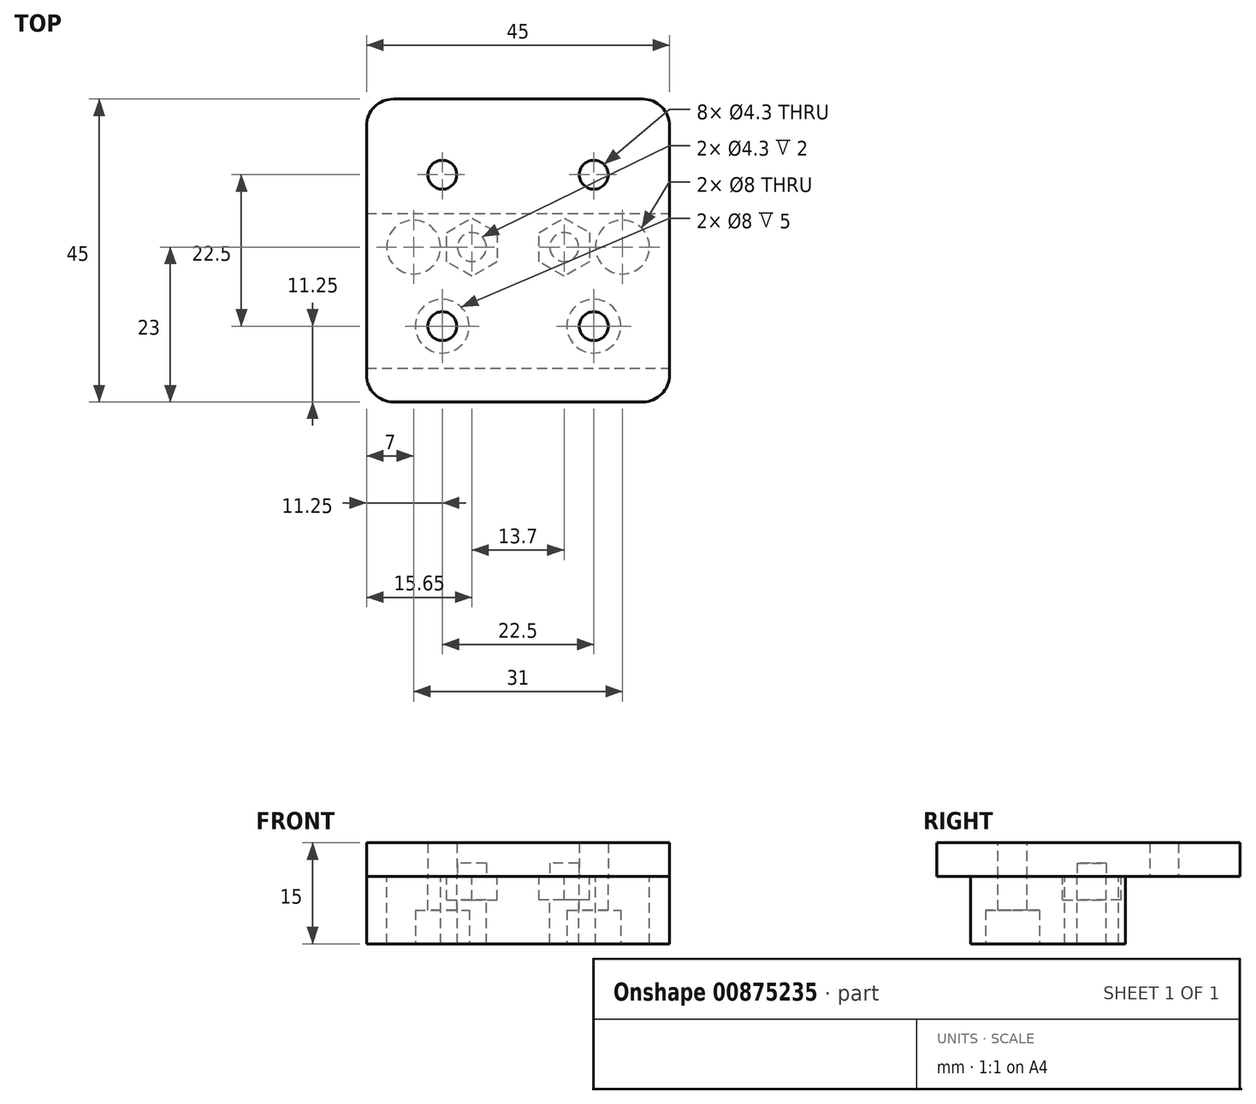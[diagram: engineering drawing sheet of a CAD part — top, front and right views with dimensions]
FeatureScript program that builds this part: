
annotation { "Feature Type Name" : "Feature", "Feature Type Description" : "" }
export const myFeature = defineFeature(function(context is Context, id is Id, definition is map)
    precondition{}
    {
        {
            var Q0;
            Q0=qCreatedBy(makeId("Top.planeOp"),FACE);
            var sketch = newSketch(context, id + "F0", { "sketchPlane" : qUnion([Q0])});
            skLineSegment(sketch, "E0.bottom", {"start": v(5, -5) * mm, "end": v(50, -5) * mm});
            skLineSegment(sketch, "E1", {"start": v(27.5, 40) * mm, "end": v(27.5, -5) * mm, "construction": true});
            skLineSegment(sketch, "E2.bottom", {"start": v(9, -5) * mm, "end": v(46, -5) * mm});
            skLineSegment(sketch, "E2.top", {"start": v(9, 40) * mm, "end": v(46, 40) * mm});
            skLineSegment(sketch, "E2.left", {"start": v(5, -1) * mm, "end": v(5, 36) * mm});
            skLineSegment(sketch, "E2.right", {"start": v(50, -1) * mm, "end": v(50, 36) * mm});
            skLineSegment(sketch, "E3", {"start": v(18.4, 28.75) * mm, "end": v(36.6, 28.75) * mm, "construction": true});
            skLineSegment(sketch, "E4", {"start": v(38.75, 26.6) * mm, "end": v(38.75, 8.4) * mm, "construction": true});
            skLineSegment(sketch, "E5", {"start": v(36.6, 6.25) * mm, "end": v(18.4, 6.25) * mm, "construction": true});
            skLineSegment(sketch, "E6", {"start": v(16.25, 8.4) * mm, "end": v(16.25, 26.6) * mm, "construction": true});
            skPoint(sketch, "E7", {"position": v(27.5, 28.75) * mm});
            skPoint(sketch, "E8", {"position": v(27.5, 6.25) * mm});
            skPoint(sketch, "E9", {"position": v(50, 17.5) * mm});
            skPoint(sketch, "E10", {"position": v(5, 17.5) * mm});
            skLineSegment(sketch, "E11", {"start": v(5, 17.5) * mm, "end": v(50, 17.5) * mm, "construction": true});
            skPoint(sketch, "E12", {"position": v(16.25, 17.5) * mm});
            skPoint(sketch, "E13", {"position": v(38.75, 17.5) * mm});
            skCircle(sketch, "E14", {"center": v(16.25, 28.75) * mm, "radius": 2.15 * mm});
            skCircle(sketch, "E15", {"center": v(38.75, 6.25) * mm, "radius": 2.15 * mm});
            skCircle(sketch, "E16", {"center": v(16.25, 6.25) * mm, "radius": 2.15 * mm});
            skCircle(sketch, "E17", {"center": v(38.75, 28.75) * mm, "radius": 2.15 * mm});
            skPoint(sketch, "E18.visualSharp", {"position": v(5, 40) * mm});
            skArc(sketch, "E18.filletArc", {"start": v(9, 40) * mm, "mid": v(6.17, 38.83) * mm, "end": v(5, 36) * mm});
            skPoint(sketch, "E19.visualSharp", {"position": v(50, 40) * mm});
            skArc(sketch, "E19.filletArc", {"start": v(50, 36) * mm, "mid": v(48.83, 38.83) * mm, "end": v(46, 40) * mm});
            skPoint(sketch, "E20.visualSharp", {"position": v(50, -5) * mm});
            skArc(sketch, "E20.filletArc", {"start": v(46, -5) * mm, "mid": v(48.83, -3.83) * mm, "end": v(50, -1) * mm});
            skPoint(sketch, "E21.visualSharp", {"position": v(5, -5) * mm});
            skArc(sketch, "E21.filletArc", {"start": v(5, -1) * mm, "mid": v(6.17, -3.83) * mm, "end": v(9, -5) * mm});
            skSolve(sketch);
        }
        {
            var Q0;
            Q0=qCreatedBy(makeId("Top.planeOp"),FACE);
            var sketch = newSketch(context, id + "F1", { "sketchPlane" : qUnion([Q0])});
            skLineSegment(sketch, "E22.bottom", {"start": v(5, 0) * mm, "end": v(50, 0) * mm});
            skLineSegment(sketch, "E22.top", {"start": v(5, 23) * mm, "end": v(50, 23) * mm});
            skLineSegment(sketch, "E23", {"start": v(27.5, 23) * mm, "end": v(27.5, -48.49) * mm, "construction": true});
            skCircle(sketch, "E24", {"center": v(34.35, 18) * mm, "radius": 2.15 * mm});
            skCircle(sketch, "E25", {"center": v(20.65, 18) * mm, "radius": 2.15 * mm});
            skCircle(sketch, "E26", {"center": v(43, 18) * mm, "radius": 4 * mm});
            skCircle(sketch, "E27", {"center": v(12, 18) * mm, "radius": 4 * mm});
            skCircle(sketch, "E28.cCircle", {"center": v(20.65, 18) * mm, "radius": 3.75 * mm, "construction": true});
            skLineSegment(sketch, "E28.0", {"start": v(24.4, 20.17) * mm, "end": v(24.4, 15.83) * mm});
            skLineSegment(sketch, "E28.1", {"start": v(24.4, 15.83) * mm, "end": v(20.65, 13.67) * mm});
            skLineSegment(sketch, "E28.2", {"start": v(20.65, 13.67) * mm, "end": v(16.9, 15.83) * mm});
            skLineSegment(sketch, "E28.3", {"start": v(16.9, 15.83) * mm, "end": v(16.9, 20.17) * mm});
            skLineSegment(sketch, "E28.4", {"start": v(16.9, 20.17) * mm, "end": v(20.65, 22.33) * mm});
            skLineSegment(sketch, "E28.5", {"start": v(20.65, 22.33) * mm, "end": v(24.4, 20.17) * mm});
            skPoint(sketch, "E28.0.midPoint", {"position": v(24.4, 18) * mm});
            skCircle(sketch, "E29.cCircle", {"center": v(34.35, 18) * mm, "radius": 3.75 * mm, "construction": true});
            skLineSegment(sketch, "E29.0", {"start": v(30.6, 15.83) * mm, "end": v(30.6, 20.17) * mm});
            skLineSegment(sketch, "E29.1", {"start": v(30.6, 20.17) * mm, "end": v(34.35, 22.33) * mm});
            skLineSegment(sketch, "E29.2", {"start": v(34.35, 22.33) * mm, "end": v(38.1, 20.17) * mm});
            skLineSegment(sketch, "E29.3", {"start": v(38.1, 20.17) * mm, "end": v(38.1, 15.83) * mm});
            skLineSegment(sketch, "E29.4", {"start": v(38.1, 15.83) * mm, "end": v(34.35, 13.67) * mm});
            skLineSegment(sketch, "E29.5", {"start": v(34.35, 13.67) * mm, "end": v(30.6, 15.83) * mm});
            skPoint(sketch, "E29.0.midPoint", {"position": v(30.6, 18) * mm});
            skLineSegment(sketch, "E30.0", {"start": v(5, -1) * mm, "end": v(5, 36) * mm, "construction": true});
            skLineSegment(sketch, "E31.0", {"start": v(50, -1) * mm, "end": v(50, 36) * mm, "construction": true});
            skLineSegment(sketch, "E32", {"start": v(5, 0) * mm, "end": v(5, 23) * mm});
            skLineSegment(sketch, "E33", {"start": v(50, 23) * mm, "end": v(50, 0) * mm});
            skSolve(sketch);
        }
        {
            var Q0;
            {var subQ0=sQuery(id+"F0.wireOp",EDGE,"E0.top");Q0=makeQuery(id+"F0.imprint","IMPRINT",FACE,{"disambiguationData":[TD([[makeQuery(id+"F0.imprint","IMPRINT",EDGE,{"derivedFrom":subQ0}),1.0]])]});}
            var Q1;
            {var subQ0=sQuery(id+"F0.wireOp",EDGE,"E0.top");Q1=makeQuery(id+"F0.imprint","IMPRINT",FACE,{"disambiguationData":[TD([[makeQuery(id+"F0.imprint","IMPRINT",EDGE,{"derivedFrom":subQ0}),-1.0]])]});}
            var Q2;
            Q2=makeQuery(id+"F0.imprint","IMPRINT",FACE,{"disambiguationData":[TD([[makeQuery(id+"F0.imprint","IMPRINT",EDGE,{"derivedFrom":sQuery(id+"F0.wireOp",EDGE,"E2.top")}),-1.0]])]});
            var Q3;
            Q3=makeQuery(id+"F0.imprint","IMPRINT",FACE,{"disambiguationData":[TD([[makeQuery(id+"F0.imprint","IMPRINT",EDGE,{"derivedFrom":sQuery(id+"F0.wireOp",EDGE,"E16")}),1.0]])]});
            var Q4;
            Q4=makeQuery(id+"F0.imprint","IMPRINT",FACE,{"disambiguationData":[TD([[makeQuery(id+"F0.imprint","IMPRINT",EDGE,{"derivedFrom":sQuery(id+"F0.wireOp",EDGE,"E15")}),1.0]])]});
            extrude(context, id + "F2", {"entities" : qUnion([Q0, Q1, Q2, Q3, Q4]), "depth" : 5 * mm, "offsetDistance" : 25 * mm});
        }
        {
            var Q0;
            Q0=makeQuery(id+"F1.imprint","IMPRINT",FACE,{"disambiguationData":[TD([[makeQuery(id+"F1.imprint","IMPRINT",EDGE,{"derivedFrom":sQuery(id+"F1.wireOp",EDGE,"E22.bottom")}),1.0]])]});
            var Q1;
            Q1=makeQuery(id+"F1.imprint","IMPRINT",FACE,{"disambiguationData":[TD([[makeQuery(id+"F1.imprint","IMPRINT",EDGE,{"derivedFrom":sQuery(id+"F1.wireOp",EDGE,"E25")}),-1.0]])]});
            var Q2;
            Q2=makeQuery(id+"F1.imprint","IMPRINT",FACE,{"disambiguationData":[TD([[makeQuery(id+"F1.imprint","IMPRINT",EDGE,{"derivedFrom":sQuery(id+"F1.wireOp",EDGE,"E24")}),-1.0]])]});
            extrude(context, id + "F3", {"entities" : qUnion([Q0, Q1, Q2]), "depth" : -10 * mm, "offsetDistance" : 25 * mm});
        }
        {
            var Q0;
            Q0=makeQuery(id+"F1.imprint","IMPRINT",FACE,{"disambiguationData":[TD([[makeQuery(id+"F1.imprint","IMPRINT",EDGE,{"derivedFrom":sQuery(id+"F1.wireOp",EDGE,"E25")}),-1.0]])]});
            var Q1;
            Q1=makeQuery(id+"F1.imprint","IMPRINT",FACE,{"disambiguationData":[TD([[makeQuery(id+"F1.imprint","IMPRINT",EDGE,{"derivedFrom":sQuery(id+"F1.wireOp",EDGE,"E24")}),-1.0]])]});
            extrude(context, id + "F4", {"entities" : qUnion([Q0, Q1]), "operationType" : NewBodyOperationType.REMOVE, "oppositeDirection" : true, "depth" : 3.5 * mm, "offsetDistance" : 25 * mm});
        }
        {
            var Q0;
            Q0=makeQuery(id+"F1.imprint","IMPRINT",FACE,{"disambiguationData":[TD([[makeQuery(id+"F1.imprint","IMPRINT",EDGE,{"derivedFrom":sQuery(id+"F1.wireOp",EDGE,"E24")}),1.0]])]});
            var Q1;
            Q1=makeQuery(id+"F1.imprint","IMPRINT",FACE,{"disambiguationData":[TD([[makeQuery(id+"F1.imprint","IMPRINT",EDGE,{"derivedFrom":sQuery(id+"F1.wireOp",EDGE,"E25")}),1.0]])]});
            var Q2;
            Q2=sQuery(id+"F1.wireOp",EDGE,"E24");
            var Q3;
            Q3=sQuery(id+"F1.wireOp",EDGE,"E25");
            extrude(context, id + "F5", {"entities" : qUnion([Q0, Q1]), "operationType" : NewBodyOperationType.REMOVE, "surfaceEntities" : qUnion([Q2, Q3]), "oppositeDirection" : true, "depth" : -2 * mm, "offsetDistance" : 25 * mm});
        }
        {
            var Q0;
            Q0=makeQuery(id+"F0.imprint","IMPRINT",FACE,{"disambiguationData":[TD([[makeQuery(id+"F0.imprint","IMPRINT",EDGE,{"derivedFrom":sQuery(id+"F0.wireOp",EDGE,"E16")}),1.0]])]});
            var Q1;
            Q1=makeQuery(id+"F0.imprint","IMPRINT",FACE,{"disambiguationData":[TD([[makeQuery(id+"F0.imprint","IMPRINT",EDGE,{"derivedFrom":sQuery(id+"F0.wireOp",EDGE,"E15")}),1.0]])]});
            var Q2;
            Q2=sQuery(id+"F0.wireOp",EDGE,"E16");
            var Q3;
            Q3=sQuery(id+"F0.wireOp",EDGE,"E15");
            extrude(context, id + "F6", {"entities" : qUnion([Q0, Q1]), "operationType" : NewBodyOperationType.REMOVE, "surfaceEntities" : qUnion([Q2, Q3]), "endBound" : BoundingType.SYMMETRIC, "oppositeDirection" : true, "depth" : 20 * mm, "offsetDistance" : 25 * mm});
        }
        {
            var Q0;
            Q0=makeQuery(id+"F3.opExtrude","CAP_FACE",FACE,{"disambiguationData":[OSD([sQuery(id+"F1.wireOp",EDGE,"E22.bottom"),sQuery(id+"F1.wireOp",EDGE,"E22.top"),sQuery(id+"F1.wireOp",EDGE,"E24"),sQuery(id+"F1.wireOp",EDGE,"E25"),sQuery(id+"F1.wireOp",EDGE,"E26"),sQuery(id+"F1.wireOp",EDGE,"E27"),sQuery(id+"F1.wireOp",EDGE,"E32"),sQuery(id+"F1.wireOp",EDGE,"E33")])],"isStart":false});
            var sketch = newSketch(context, id + "F7", { "sketchPlane" : qUnion([Q0])});
            skCircle(sketch, "E34", {"center": v(16.25, -6.25) * mm, "radius": 4 * mm});
            skCircle(sketch, "E35", {"center": v(38.75, -6.25) * mm, "radius": 4 * mm});
            skSolve(sketch);
        }
        {
            var Q0;
            Q0=makeQuery(id+"F7.imprint","IMPRINT",FACE,{"disambiguationData":[TD([[makeQuery(id+"F7.imprint","IMPRINT",EDGE,{"derivedFrom":sQuery(id+"F7.wireOp",EDGE,"E34")}),1.0]])]});
            var Q1;
            Q1=makeQuery(id+"F7.imprint","IMPRINT",FACE,{"disambiguationData":[TD([[makeQuery(id+"F7.imprint","IMPRINT",EDGE,{"derivedFrom":sQuery(id+"F7.wireOp",EDGE,"E35")}),1.0]])]});
            extrude(context, id + "F8", {"entities" : qUnion([Q0, Q1]), "operationType" : NewBodyOperationType.REMOVE, "oppositeDirection" : true, "depth" : 5 * mm, "offsetDistance" : 25 * mm});
        }
    });
